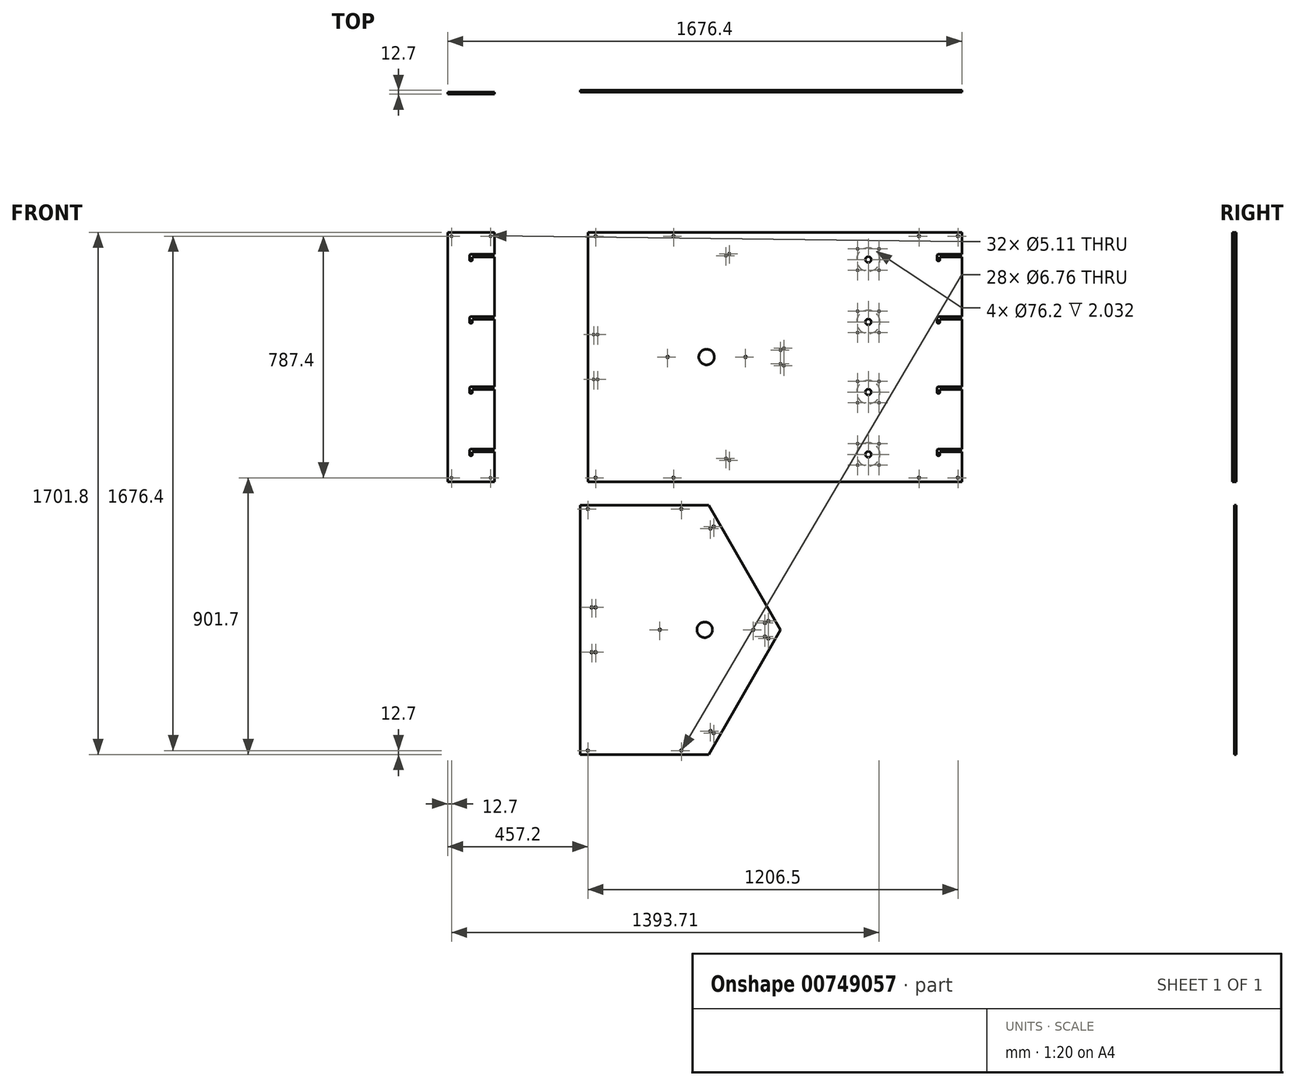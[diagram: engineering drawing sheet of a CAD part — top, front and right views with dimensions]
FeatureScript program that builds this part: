
annotation { "Feature Type Name" : "Feature", "Feature Type Description" : "" }
export const myFeature = defineFeature(function(context is Context, id is Id, definition is map)
    precondition{}
    {
        {
            var Q0;
            Q0=qCreatedBy(makeId("Front.planeOp"),FACE);
            var sketch = newSketch(context, id + "F0", { "sketchPlane" : qUnion([Q0])});
            skLineSegment(sketch, "E0.bottom", {"start": v(0, 0) * mm, "end": v(1219.2, 0) * mm});
            skLineSegment(sketch, "E0.top", {"start": v(53.97, 812.8) * mm, "end": v(1219.2, 812.8) * mm});
            skLineSegment(sketch, "E0.left", {"start": v(0, 0) * mm, "end": v(0, 47.62) * mm});
            skLineSegment(sketch, "E0.right", {"start": v(1219.2, 0) * mm, "end": v(1219.2, 812.8) * mm});
            skLineSegment(sketch, "E1.trimOffspring", {"start": v(0, 104.78) * mm, "end": v(0, 406.4) * mm});
            skLineSegment(sketch, "E2", {"start": v(53.97, 812.8) * mm, "end": v(0, 812.8) * mm});
            skLineSegment(sketch, "E3", {"start": v(0, 812.8) * mm, "end": v(0, 406.4) * mm});
            skLineSegment(sketch, "E4", {"start": v(0, 104.78) * mm, "end": v(0, 47.62) * mm});
            skLineSegment(sketch, "E5", {"start": v(1219.2, 406.4) * mm, "end": v(0, 406.4) * mm, "construction": true});
            skLineSegment(sketch, "E6.left", {"start": v(0, 508) * mm, "end": v(0, 304.8) * mm});
            skSolve(sketch);
        }
        {
            var Q0;
            Q0 = qSketchRegion(id + "F0", true);
            extrude(context, id + "F1", {"entities" : qUnion([Q0]), "oppositeDirection" : true, "depth" : 6.35 * mm, "offsetDistance" : 25.4 * mm});
        }
        {
            var Q0;
            Q0=makeQuery(id+"F1.opExtrude","CAP_FACE",FACE,{"disambiguationData":[OSD([sQuery(id+"F0.wireOp",EDGE,"E0.bottom"),sQuery(id+"F0.wireOp",EDGE,"E0.top"),sQuery(id+"F0.wireOp",EDGE,"E0.left"),sQuery(id+"F0.wireOp",EDGE,"E0.right"),sQuery(id+"F0.wireOp",EDGE,"GyBe3EqK-cSh5-v1t1-OVTD-ahxNfT15hAsZ.top"),sQuery(id+"F0.wireOp",EDGE,"GyBe3EqK-cSh5-v1t1-OVTD-ahxNfT15hAsZ.right"),sQuery(id+"F0.wireOp",EDGE,"EnS1OxtH-lJOK-UO4v-DnPg-Mq8DwQejlwmV.bottom"),sQuery(id+"F0.wireOp",EDGE,"EnS1OxtH-lJOK-UO4v-DnPg-Mq8DwQejlwmV.top"),sQuery(id+"F0.wireOp",EDGE,"EnS1OxtH-lJOK-UO4v-DnPg-Mq8DwQejlwmV.right"),sQuery(id+"F0.wireOp",EDGE,"E1.trimOffspring")])],"isStart":true});
            var sketch = newSketch(context, id + "F2", { "sketchPlane" : qUnion([Q0])});
            skLineSegment(sketch, "E7", {"start": v(1219.2, 406.4) * mm, "end": v(0, 406.4) * mm, "construction": true});
            skLineSegment(sketch, "E8", {"start": v(406.4, 0) * mm, "end": v(641.04, 406.4) * mm, "construction": true});
            skLineSegment(sketch, "E9", {"start": v(641.04, 406.4) * mm, "end": v(406.4, 812.8) * mm, "construction": true});
            skPoint(sketch, "E10", {"position": v(450.4, 76.2) * mm});
            skPoint(sketch, "E11", {"position": v(628.2, 384.16) * mm});
            skLineSegment(sketch, "E12", {"start": v(421.06, 0) * mm, "end": v(655.7, 406.4) * mm, "construction": true});
            skLineSegment(sketch, "E13", {"start": v(450.4, 76.2) * mm, "end": v(461.4, 69.85) * mm, "construction": true});
            skLineSegment(sketch, "E14", {"start": v(628.2, 384.16) * mm, "end": v(639.2, 377.8) * mm, "construction": true});
            skPoint(sketch, "E15", {"position": v(639.2, 377.8) * mm});
            skPoint(sketch, "E16", {"position": v(461.4, 69.85) * mm});
            skPoint(sketch, "E17.MirrorP", {"position": v(628.2, 428.64) * mm});
            skPoint(sketch, "E18.MirrorP", {"position": v(639.2, 435) * mm});
            skPoint(sketch, "E19.MirrorP", {"position": v(461.4, 742.95) * mm});
            skPoint(sketch, "E20.MirrorP", {"position": v(450.4, 736.6) * mm});
            skLineSegment(sketch, "E21", {"start": v(25.4, 812.8) * mm, "end": v(25.4, 0) * mm, "construction": true});
            skPoint(sketch, "E22", {"position": v(19.05, 479.43) * mm});
            skPoint(sketch, "E23.MirrorP", {"position": v(31.75, 479.43) * mm});
            skPoint(sketch, "E24.MirrorP", {"position": v(19.05, 333.38) * mm});
            skPoint(sketch, "E25.MirrorP", {"position": v(31.75, 333.38) * mm});
            skSolve(sketch);
        }
        {
            var Q0;
            Q0=sQuery(id+"F2.wireOp",VERTEX,"1f2a52ec-5eff-4167-b222-c35b7b9c67ac0.MirrorP");
            var Q1;
            Q1=sQuery(id+"F2.wireOp",VERTEX,"6a59a917-cddb-4341-b7b2-614a49050ed80.MirrorP");
            var Q2;
            Q2=sQuery(id+"F2.wireOp",VERTEX,"aa4bf911-a7ad-4460-99d6-e9a0e6d8d9e1");
            var Q3;
            Q3=sQuery(id+"F2.wireOp",VERTEX,"df6880c4-e116-4ecd-98e9-50faa79850ba");
            var Q4;
            Q4=sQuery(id+"F2.wireOp",VERTEX,"cc07dee6-96a4-47fe-b955-c56ce8794536");
            var Q5;
            Q5=sQuery(id+"F2.wireOp",VERTEX,"bf74a886-9e41-4cef-b4e5-6878ea112274");
            var Q6;
            Q6=sQuery(id+"F2.wireOp",VERTEX,"cd125775-8d29-4c7f-8b29-d38cd7ae1aca0.MirrorP");
            var Q7;
            Q7=sQuery(id+"F2.wireOp",VERTEX,"78534849-580e-4fdc-a252-b2fe906053fd0.MirrorP");
            var Q8;
            Q8=sQuery(id+"F2.wireOp",VERTEX,"19cf28b5-96e7-4680-8611-90bc4ffa497d0.MirrorP");
            var Q9;
            Q9=sQuery(id+"F2.wireOp",VERTEX,"6d1cc372-7a9e-40b0-874d-be10c53de4300.MirrorP");
            var Q10;
            Q10=sQuery(id+"F2.wireOp",VERTEX,"eb98779b-e2d4-40db-b351-41a48d78d36b0.MirrorP");
            var Q11;
            Q11=sQuery(id+"F2.wireOp",VERTEX,"24989635-3b41-4970-88e9-65368ecc07f30.MirrorP");
            var Q12;
            Q12=sQuery(id+"F2.wireOp",VERTEX,"E10");
            var Q13;
            Q13=sQuery(id+"F2.wireOp",VERTEX,"E16");
            var Q14;
            Q14=sQuery(id+"F2.wireOp",VERTEX,"E15");
            var Q15;
            Q15=sQuery(id+"F2.wireOp",VERTEX,"E11");
            var Q16;
            Q16=sQuery(id+"F2.wireOp",VERTEX,"E18.MirrorP");
            var Q17;
            Q17=sQuery(id+"F2.wireOp",VERTEX,"E17.MirrorP");
            var Q18;
            Q18=sQuery(id+"F2.wireOp",VERTEX,"E19.MirrorP");
            var Q19;
            Q19=sQuery(id+"F2.wireOp",VERTEX,"E20.MirrorP");
            var Q20;
            Q20=sQuery(id+"F2.wireOp",VERTEX,"E25.MirrorP");
            var Q21;
            Q21=sQuery(id+"F2.wireOp",VERTEX,"E22");
            var Q22;
            Q22=sQuery(id+"F2.wireOp",VERTEX,"E23.MirrorP");
            var Q23;
            Q23=sQuery(id+"F2.wireOp",VERTEX,"E24.MirrorP");
            var Q24;
            Q24=makeQuery(id+"F1.opExtrude","SWEPT_BODY",BODY,{"disambiguationData":[OSD([sQuery(id+"F0.wireOp",EDGE,"E0.bottom"),sQuery(id+"F0.wireOp",EDGE,"E0.top"),sQuery(id+"F0.wireOp",EDGE,"E0.left"),sQuery(id+"F0.wireOp",EDGE,"E0.right"),sQuery(id+"F0.wireOp",EDGE,"GyBe3EqK-cSh5-v1t1-OVTD-ahxNfT15hAsZ.top"),sQuery(id+"F0.wireOp",EDGE,"GyBe3EqK-cSh5-v1t1-OVTD-ahxNfT15hAsZ.right"),sQuery(id+"F0.wireOp",EDGE,"EnS1OxtH-lJOK-UO4v-DnPg-Mq8DwQejlwmV.bottom"),sQuery(id+"F0.wireOp",EDGE,"EnS1OxtH-lJOK-UO4v-DnPg-Mq8DwQejlwmV.top"),sQuery(id+"F0.wireOp",EDGE,"EnS1OxtH-lJOK-UO4v-DnPg-Mq8DwQejlwmV.right"),sQuery(id+"F0.wireOp",EDGE,"E1.trimOffspring")])]});
            hole(context, id + "F3", {"style" : HoleStyle.SIMPLE, "endStyle" : HoleEndStyle.BLIND, "standardTappedOrClearance" : lookupTablePath({ "standard" : "ANSI", "engagement" : "75%", "pitch" : "20 tpi", "size" : "1/4", "type" : "Tapped" }), "standardBlindInLast" : lookupTablePath({ "standard" : "ANSI", "engagement" : "75%", "pitch" : "20 tpi", "size" : "1/4", "type" : "Tapped" }), "holeDiameter" : 5.1 * mm, "majorDiameter" : 6.35 * mm, "showTappedDepth" : true, "holeDepth" : 26.06 * mm, "isTappedThrough" : true, "tappedDepth" : 22.25 * mm, "tapClearance" : 3, "locations" : qUnion([Q0, Q1, Q2, Q3, Q4, Q5, Q6, Q7, Q8, Q9, Q10, Q11, Q12, Q13, Q14, Q15, Q16, Q17, Q18, Q19, Q20, Q21, Q22, Q23]), "scope" : qUnion([Q24])});
        }
        {
            var Q0;
            Q0=makeQuery(id+"F1.opExtrude","CAP_FACE",FACE,{"disambiguationData":[OSD([sQuery(id+"F0.wireOp",EDGE,"E0.bottom"),sQuery(id+"F0.wireOp",EDGE,"E0.top"),sQuery(id+"F0.wireOp",EDGE,"E0.left"),sQuery(id+"F0.wireOp",EDGE,"E0.right"),sQuery(id+"F0.wireOp",EDGE,"GyBe3EqK-cSh5-v1t1-OVTD-ahxNfT15hAsZ.top"),sQuery(id+"F0.wireOp",EDGE,"GyBe3EqK-cSh5-v1t1-OVTD-ahxNfT15hAsZ.right"),sQuery(id+"F0.wireOp",EDGE,"EnS1OxtH-lJOK-UO4v-DnPg-Mq8DwQejlwmV.bottom"),sQuery(id+"F0.wireOp",EDGE,"EnS1OxtH-lJOK-UO4v-DnPg-Mq8DwQejlwmV.top"),sQuery(id+"F0.wireOp",EDGE,"EnS1OxtH-lJOK-UO4v-DnPg-Mq8DwQejlwmV.right"),sQuery(id+"F0.wireOp",EDGE,"E1.trimOffspring")])],"isStart":true});
            var sketch = newSketch(context, id + "F4", { "sketchPlane" : qUnion([Q0])});
            skLineSegment(sketch, "E26", {"start": v(1219.2, 406.4) * mm, "end": v(0, 406.4) * mm, "construction": true});
            skLineSegment(sketch, "E27", {"start": v(1219.2, 736.6) * mm, "end": v(1143, 736.6) * mm});
            skLineSegment(sketch, "E28", {"start": v(1143, 736.6) * mm, "end": v(1143, 723.9) * mm});
            skArc(sketch, "E29.0.startCap", {"start": v(1219.2, 741.36) * mm, "mid": v(1223.96, 736.6) * mm, "end": v(1219.2, 731.84) * mm});
            skArc(sketch, "E29.0.endCap", {"start": v(1143, 731.84) * mm, "mid": v(1138.24, 736.6) * mm, "end": v(1143, 741.36) * mm});
            skLineSegment(sketch, "E29.0.left", {"start": v(1219.2, 731.84) * mm, "end": v(1143, 731.84) * mm});
            skLineSegment(sketch, "E29.0.right", {"start": v(1219.2, 741.36) * mm, "end": v(1143, 741.36) * mm});
            skArc(sketch, "E29.1.startCap", {"start": v(1138.24, 736.6) * mm, "mid": v(1143, 741.36) * mm, "end": v(1147.76, 736.6) * mm});
            skArc(sketch, "E29.1.endCap", {"start": v(1147.76, 723.9) * mm, "mid": v(1143, 719.14) * mm, "end": v(1138.24, 723.9) * mm});
            skLineSegment(sketch, "E29.1.left", {"start": v(1147.76, 736.6) * mm, "end": v(1147.76, 723.9) * mm});
            skLineSegment(sketch, "E29.1.right", {"start": v(1138.24, 736.6) * mm, "end": v(1138.24, 723.9) * mm});
            skLineSegment(sketch, "E30", {"start": v(1219.2, 533.4) * mm, "end": v(1143, 533.4) * mm});
            skLineSegment(sketch, "E31", {"start": v(1143, 533.4) * mm, "end": v(1143, 520.7) * mm});
            skArc(sketch, "E32.0.startCap", {"start": v(1219.2, 538.16) * mm, "mid": v(1223.96, 533.4) * mm, "end": v(1219.2, 528.64) * mm});
            skArc(sketch, "E32.0.endCap", {"start": v(1143, 528.64) * mm, "mid": v(1138.24, 533.4) * mm, "end": v(1143, 538.16) * mm});
            skLineSegment(sketch, "E32.0.left", {"start": v(1219.2, 528.64) * mm, "end": v(1143, 528.64) * mm});
            skLineSegment(sketch, "E32.0.right", {"start": v(1219.2, 538.16) * mm, "end": v(1143, 538.16) * mm});
            skArc(sketch, "E32.1.startCap", {"start": v(1138.24, 533.4) * mm, "mid": v(1143, 538.16) * mm, "end": v(1147.76, 533.4) * mm});
            skArc(sketch, "E32.1.endCap", {"start": v(1147.76, 520.7) * mm, "mid": v(1143, 515.94) * mm, "end": v(1138.24, 520.7) * mm});
            skLineSegment(sketch, "E32.1.left", {"start": v(1147.76, 533.4) * mm, "end": v(1147.76, 520.7) * mm});
            skLineSegment(sketch, "E32.1.right", {"start": v(1138.24, 533.4) * mm, "end": v(1138.24, 520.7) * mm});
            skLineSegment(sketch, "E33", {"start": v(0, 622.3) * mm, "end": v(1219.2, 622.3) * mm, "construction": true});
            skLineSegment(sketch, "E34", {"start": v(0, 190.5) * mm, "end": v(1219.2, 190.5) * mm, "construction": true});
            skLineSegment(sketch, "E35", {"start": v(1219.2, 304.8) * mm, "end": v(1143, 304.8) * mm});
            skLineSegment(sketch, "E36", {"start": v(1143, 304.8) * mm, "end": v(1143, 292.1) * mm});
            skArc(sketch, "E37.0.startCap", {"start": v(1219.2, 309.56) * mm, "mid": v(1223.96, 304.8) * mm, "end": v(1219.2, 300.04) * mm});
            skArc(sketch, "E37.0.endCap", {"start": v(1143, 300.04) * mm, "mid": v(1138.24, 304.8) * mm, "end": v(1143, 309.56) * mm});
            skLineSegment(sketch, "E37.0.left", {"start": v(1219.2, 300.04) * mm, "end": v(1143, 300.04) * mm});
            skLineSegment(sketch, "E37.0.right", {"start": v(1219.2, 309.56) * mm, "end": v(1143, 309.56) * mm});
            skArc(sketch, "E37.1.startCap", {"start": v(1138.24, 304.8) * mm, "mid": v(1143, 309.56) * mm, "end": v(1147.76, 304.8) * mm});
            skArc(sketch, "E37.1.endCap", {"start": v(1147.76, 292.1) * mm, "mid": v(1143, 287.34) * mm, "end": v(1138.24, 292.1) * mm});
            skLineSegment(sketch, "E37.1.left", {"start": v(1147.76, 304.8) * mm, "end": v(1147.76, 292.1) * mm});
            skLineSegment(sketch, "E37.1.right", {"start": v(1138.24, 304.8) * mm, "end": v(1138.24, 292.1) * mm});
            skLineSegment(sketch, "E38", {"start": v(1219.2, 101.6) * mm, "end": v(1143, 101.6) * mm});
            skLineSegment(sketch, "E39", {"start": v(1143, 101.6) * mm, "end": v(1143, 88.9) * mm});
            skArc(sketch, "E40.0.startCap", {"start": v(1219.2, 106.36) * mm, "mid": v(1223.96, 101.6) * mm, "end": v(1219.2, 96.84) * mm});
            skArc(sketch, "E40.0.endCap", {"start": v(1143, 96.84) * mm, "mid": v(1138.24, 101.6) * mm, "end": v(1143, 106.36) * mm});
            skLineSegment(sketch, "E40.0.left", {"start": v(1219.2, 96.84) * mm, "end": v(1143, 96.84) * mm});
            skLineSegment(sketch, "E40.0.right", {"start": v(1219.2, 106.36) * mm, "end": v(1143, 106.36) * mm});
            skArc(sketch, "E40.1.startCap", {"start": v(1138.24, 101.6) * mm, "mid": v(1143, 106.36) * mm, "end": v(1147.76, 101.6) * mm});
            skArc(sketch, "E40.1.endCap", {"start": v(1147.76, 88.9) * mm, "mid": v(1143, 84.14) * mm, "end": v(1138.24, 88.9) * mm});
            skLineSegment(sketch, "E40.1.left", {"start": v(1147.76, 101.6) * mm, "end": v(1147.76, 88.9) * mm});
            skLineSegment(sketch, "E40.1.right", {"start": v(1138.24, 101.6) * mm, "end": v(1138.24, 88.9) * mm});
            skSolve(sketch);
        }
        {
            var Q0;
            Q0 = qSketchRegion(id + "F4", true);
            extrude(context, id + "F5", {"entities" : qUnion([Q0]), "operationType" : NewBodyOperationType.REMOVE, "oppositeDirection" : true, "depth" : 25.4 * mm, "offsetDistance" : 25.4 * mm});
        }
        {
            var Q0;
            Q0=makeQuery(id+"F1.opExtrude","CAP_FACE",FACE,{"disambiguationData":[OSD([sQuery(id+"F0.wireOp",EDGE,"E0.bottom"),sQuery(id+"F0.wireOp",EDGE,"E0.top"),sQuery(id+"F0.wireOp",EDGE,"E0.left"),sQuery(id+"F0.wireOp",EDGE,"E0.right"),sQuery(id+"F0.wireOp",EDGE,"E1.trimOffspring"),sQuery(id+"F0.wireOp",EDGE,"E2"),sQuery(id+"F0.wireOp",EDGE,"E3"),sQuery(id+"F0.wireOp",EDGE,"E4")])],"isStart":true});
            var sketch = newSketch(context, id + "F6", { "sketchPlane" : qUnion([Q0])});
            skLineSegment(sketch, "E41", {"start": v(0, 0) * mm, "end": v(234.64, 406.4) * mm, "construction": true});
            skLineSegment(sketch, "E42", {"start": v(234.64, 406.4) * mm, "end": v(0, 812.8) * mm, "construction": true});
            skLineSegment(sketch, "E43", {"start": v(304.8, 812.8) * mm, "end": v(539.44, 406.4) * mm, "construction": true});
            skLineSegment(sketch, "E44", {"start": v(539.44, 406.4) * mm, "end": v(304.8, 0) * mm, "construction": true});
            skLineSegment(sketch, "E45", {"start": v(234.64, 406.4) * mm, "end": v(539.44, 406.4) * mm, "construction": true});
            skLineSegment(sketch, "E46", {"start": v(152.4, 0) * mm, "end": v(152.4, 812.8) * mm, "construction": true});
            skPoint(sketch, "E47", {"position": v(25.4, 12.7) * mm});
            skLineSegment(sketch, "E48", {"start": v(387.04, 670.36) * mm, "end": v(387.04, 142.44) * mm, "construction": true});
            skPoint(sketch, "E48.startSnap0", {"position": v(387.04, 406.4) * mm});
            skPoint(sketch, "E49", {"position": v(514.04, 406.4) * mm});
            skPoint(sketch, "E50.MirrorP", {"position": v(279.4, 12.7) * mm});
            skPoint(sketch, "E51.MirrorP", {"position": v(279.4, 800.1) * mm});
            skPoint(sketch, "E52.MirrorP", {"position": v(25.4, 800.1) * mm});
            skPoint(sketch, "E53.MirrorP", {"position": v(260.04, 406.4) * mm});
            skCircle(sketch, "E54", {"center": v(387.04, 406.4) * mm, "radius": 25.4 * mm});
            skSolve(sketch);
        }
        {
            var Q0;
            Q0=sQuery(id+"F6.wireOp",VERTEX,"E52.MirrorP");
            var Q1;
            Q1=sQuery(id+"F6.wireOp",VERTEX,"E51.MirrorP");
            var Q2;
            Q2=sQuery(id+"F6.wireOp",VERTEX,"E47");
            var Q3;
            Q3=sQuery(id+"F6.wireOp",VERTEX,"E50.MirrorP");
            var Q4;
            Q4=sQuery(id+"F6.wireOp",VERTEX,"E53.MirrorP");
            var Q5;
            Q5=sQuery(id+"F6.wireOp",VERTEX,"E49");
            var Q6;
            Q6=makeQuery(id+"F1.opExtrude","SWEPT_BODY",BODY,{"disambiguationData":[OSD([sQuery(id+"F0.wireOp",EDGE,"E0.bottom"),sQuery(id+"F0.wireOp",EDGE,"E0.top"),sQuery(id+"F0.wireOp",EDGE,"E0.left"),sQuery(id+"F0.wireOp",EDGE,"E0.right"),sQuery(id+"F0.wireOp",EDGE,"E1.trimOffspring"),sQuery(id+"F0.wireOp",EDGE,"E2"),sQuery(id+"F0.wireOp",EDGE,"E3"),sQuery(id+"F0.wireOp",EDGE,"E4")])]});
            hole(context, id + "F7", {"style" : HoleStyle.SIMPLE, "endStyle" : HoleEndStyle.BLIND, "standardTappedOrClearance" : lookupTablePath({ "fit" : "Normal (ASME)", "standard" : "ANSI", "size" : "1/4", "type" : "Clearance" }), "standardBlindInLast" : lookupTablePath({ "fit" : "Free", "standard" : "ANSI", "size" : "1/4", "type" : "Clearance" }), "holeDiameter" : 6.76 * mm, "majorDiameter" : 6.35 * mm, "holeDepth" : 26.06 * mm, "isTappedThrough" : true, "tappedDepth" : 22.25 * mm, "tapClearance" : 3, "locations" : qUnion([Q0, Q1, Q2, Q3, Q4, Q5]), "scope" : qUnion([Q6])});
        }
        {
            var Q0;
            Q0=qCreatedBy(makeId("Front.planeOp"),FACE);
            var sketch = newSketch(context, id + "F8", { "sketchPlane" : qUnion([Q0])});
            skLineSegment(sketch, "E55.bottom", {"start": v(-304.8, 0) * mm, "end": v(-457.2, 0) * mm});
            skLineSegment(sketch, "E55.top", {"start": v(-304.8, 812.8) * mm, "end": v(-457.2, 812.8) * mm});
            skLineSegment(sketch, "E55.left", {"start": v(-304.8, 0) * mm, "end": v(-304.8, 812.8) * mm});
            skLineSegment(sketch, "E55.right", {"start": v(-457.2, 0) * mm, "end": v(-457.2, 812.8) * mm});
            skLineSegment(sketch, "E56", {"start": v(-304.8, 406.4) * mm, "end": v(-457.2, 406.4) * mm, "construction": true});
            skLineSegment(sketch, "E57", {"start": v(-304.8, 622.3) * mm, "end": v(-457.2, 622.3) * mm, "construction": true});
            skLineSegment(sketch, "E58", {"start": v(-304.8, 190.5) * mm, "end": v(-457.2, 190.5) * mm, "construction": true});
            skLineSegment(sketch, "E59", {"start": v(-304.8, 736.6) * mm, "end": v(-381, 736.6) * mm});
            skLineSegment(sketch, "E60", {"start": v(-381, 736.6) * mm, "end": v(-381, 723.9) * mm});
            skArc(sketch, "E61.0.startCap", {"start": v(-304.8, 741.36) * mm, "mid": v(-300.04, 736.6) * mm, "end": v(-304.8, 731.84) * mm});
            skArc(sketch, "E61.0.endCap", {"start": v(-381, 731.84) * mm, "mid": v(-385.76, 736.6) * mm, "end": v(-381, 741.36) * mm});
            skLineSegment(sketch, "E61.0.left", {"start": v(-304.8, 731.84) * mm, "end": v(-381, 731.84) * mm});
            skLineSegment(sketch, "E61.0.right", {"start": v(-304.8, 741.36) * mm, "end": v(-381, 741.36) * mm});
            skArc(sketch, "E61.1.startCap", {"start": v(-385.76, 736.6) * mm, "mid": v(-381, 741.36) * mm, "end": v(-376.24, 736.6) * mm});
            skArc(sketch, "E61.1.endCap", {"start": v(-376.24, 723.9) * mm, "mid": v(-381, 719.14) * mm, "end": v(-385.76, 723.9) * mm});
            skLineSegment(sketch, "E61.1.left", {"start": v(-376.24, 736.6) * mm, "end": v(-376.24, 723.9) * mm});
            skLineSegment(sketch, "E61.1.right", {"start": v(-385.76, 736.6) * mm, "end": v(-385.76, 723.9) * mm});
            skLineSegment(sketch, "E62", {"start": v(-304.8, 533.4) * mm, "end": v(-381, 533.4) * mm});
            skLineSegment(sketch, "E63", {"start": v(-381, 533.4) * mm, "end": v(-381, 520.7) * mm});
            skArc(sketch, "E64.0.startCap", {"start": v(-304.8, 538.16) * mm, "mid": v(-300.04, 533.4) * mm, "end": v(-304.8, 528.64) * mm});
            skArc(sketch, "E64.0.endCap", {"start": v(-381, 528.64) * mm, "mid": v(-385.76, 533.4) * mm, "end": v(-381, 538.16) * mm});
            skLineSegment(sketch, "E64.0.left", {"start": v(-304.8, 528.64) * mm, "end": v(-381, 528.64) * mm});
            skLineSegment(sketch, "E64.0.right", {"start": v(-304.8, 538.16) * mm, "end": v(-381, 538.16) * mm});
            skArc(sketch, "E64.1.startCap", {"start": v(-385.76, 533.4) * mm, "mid": v(-381, 538.16) * mm, "end": v(-376.24, 533.4) * mm});
            skArc(sketch, "E64.1.endCap", {"start": v(-376.24, 520.7) * mm, "mid": v(-381, 515.94) * mm, "end": v(-385.76, 520.7) * mm});
            skLineSegment(sketch, "E64.1.left", {"start": v(-376.24, 533.4) * mm, "end": v(-376.24, 520.7) * mm});
            skLineSegment(sketch, "E64.1.right", {"start": v(-385.76, 533.4) * mm, "end": v(-385.76, 520.7) * mm});
            skLineSegment(sketch, "E65", {"start": v(-304.8, 304.8) * mm, "end": v(-381, 304.8) * mm});
            skLineSegment(sketch, "E66", {"start": v(-381, 304.8) * mm, "end": v(-381, 292.1) * mm});
            skArc(sketch, "E67.0.startCap", {"start": v(-304.8, 309.56) * mm, "mid": v(-300.04, 304.8) * mm, "end": v(-304.8, 300.04) * mm});
            skArc(sketch, "E67.0.endCap", {"start": v(-381, 300.04) * mm, "mid": v(-385.76, 304.8) * mm, "end": v(-381, 309.56) * mm});
            skLineSegment(sketch, "E67.0.left", {"start": v(-304.8, 300.04) * mm, "end": v(-381, 300.04) * mm});
            skLineSegment(sketch, "E67.0.right", {"start": v(-304.8, 309.56) * mm, "end": v(-381, 309.56) * mm});
            skArc(sketch, "E67.1.startCap", {"start": v(-385.76, 304.8) * mm, "mid": v(-381, 309.56) * mm, "end": v(-376.24, 304.8) * mm});
            skArc(sketch, "E67.1.endCap", {"start": v(-376.24, 292.1) * mm, "mid": v(-381, 287.34) * mm, "end": v(-385.76, 292.1) * mm});
            skLineSegment(sketch, "E67.1.left", {"start": v(-376.24, 304.8) * mm, "end": v(-376.24, 292.1) * mm});
            skLineSegment(sketch, "E67.1.right", {"start": v(-385.76, 304.8) * mm, "end": v(-385.76, 292.1) * mm});
            skLineSegment(sketch, "E68", {"start": v(-304.8, 101.6) * mm, "end": v(-381, 101.6) * mm});
            skLineSegment(sketch, "E69", {"start": v(-381, 101.6) * mm, "end": v(-381, 88.9) * mm});
            skArc(sketch, "E70.0.startCap", {"start": v(-304.8, 106.36) * mm, "mid": v(-300.04, 101.6) * mm, "end": v(-304.8, 96.84) * mm});
            skArc(sketch, "E70.0.endCap", {"start": v(-381, 96.84) * mm, "mid": v(-385.76, 101.6) * mm, "end": v(-381, 106.36) * mm});
            skLineSegment(sketch, "E70.0.left", {"start": v(-304.8, 96.84) * mm, "end": v(-381, 96.84) * mm});
            skLineSegment(sketch, "E70.0.right", {"start": v(-304.8, 106.36) * mm, "end": v(-381, 106.36) * mm});
            skArc(sketch, "E70.1.startCap", {"start": v(-385.76, 101.6) * mm, "mid": v(-381, 106.36) * mm, "end": v(-376.24, 101.6) * mm});
            skArc(sketch, "E70.1.endCap", {"start": v(-376.24, 88.9) * mm, "mid": v(-381, 84.14) * mm, "end": v(-385.76, 88.9) * mm});
            skLineSegment(sketch, "E70.1.left", {"start": v(-376.24, 101.6) * mm, "end": v(-376.24, 88.9) * mm});
            skLineSegment(sketch, "E70.1.right", {"start": v(-385.76, 101.6) * mm, "end": v(-385.76, 88.9) * mm});
            skLineSegment(sketch, "E71", {"start": v(-381, 812.8) * mm, "end": v(-381, 0) * mm, "construction": true});
            skPoint(sketch, "E72", {"position": v(-444.5, 12.7) * mm});
            skPoint(sketch, "E73.MirrorP", {"position": v(-444.5, 800.1) * mm});
            skPoint(sketch, "E74.MirrorP", {"position": v(-317.5, 800.1) * mm});
            skPoint(sketch, "E75.MirrorP", {"position": v(-317.5, 12.7) * mm});
            skSolve(sketch);
        }
        {
            var Q0;
            {var subQ14=sQuery(id+"F8.wireOp",EDGE,"E55.bottom");Q0=makeQuery(id+"F8.imprint","IMPRINT",FACE,{"disambiguationData":[TD([[makeQuery(id+"F8.imprint","IMPRINT",EDGE,{"derivedFrom":subQ14}),-1.0]])]});}
            extrude(context, id + "F9", {"entities" : qUnion([Q0]), "depth" : 6.35 * mm, "offsetDistance" : 25.4 * mm});
        }
        {
            var Q0;
            Q0=makeQuery(id+"F1.opExtrude","CAP_FACE",FACE,{"disambiguationData":[OSD([sQuery(id+"F0.wireOp",EDGE,"E0.bottom"),sQuery(id+"F0.wireOp",EDGE,"E0.top"),sQuery(id+"F0.wireOp",EDGE,"E0.left"),sQuery(id+"F0.wireOp",EDGE,"E0.right"),sQuery(id+"F0.wireOp",EDGE,"E1.trimOffspring"),sQuery(id+"F0.wireOp",EDGE,"E2"),sQuery(id+"F0.wireOp",EDGE,"E3"),sQuery(id+"F0.wireOp",EDGE,"E4"),sQuery(id+"F0.wireOp",EDGE,"E6.bottom"),sQuery(id+"F0.wireOp",EDGE,"E6.top"),sQuery(id+"F0.wireOp",EDGE,"E6.right")])],"isStart":false});
            var sketch = newSketch(context, id + "F10", { "sketchPlane" : qUnion([Q0])});
            skLineSegment(sketch, "E76", {"start": v(-914.4, 812.8) * mm, "end": v(-914.4, 0) * mm, "construction": true});
            skLineSegment(sketch, "E77", {"start": v(-1219.2, 622.3) * mm, "end": v(-914.4, 622.3) * mm, "construction": true});
            skCircle(sketch, "E78", {"center": v(-914.4, 723.9) * mm, "radius": 9.53 * mm});
            skCircle(sketch, "E79.MirrorC", {"center": v(-914.4, 520.7) * mm, "radius": 9.53 * mm});
            skCircle(sketch, "E80", {"center": v(-914.4, 723.9) * mm, "radius": 49.23 * mm, "construction": true});
            skLineSegment(sketch, "E81.bottom", {"start": v(-871.22, 680.72) * mm, "end": v(-957.58, 680.72) * mm, "construction": true});
            skLineSegment(sketch, "E81.top", {"start": v(-871.22, 767.08) * mm, "end": v(-957.58, 767.08) * mm, "construction": true});
            skLineSegment(sketch, "E81.left", {"start": v(-871.22, 680.72) * mm, "end": v(-871.22, 767.08) * mm, "construction": true});
            skLineSegment(sketch, "E81.right", {"start": v(-957.58, 680.72) * mm, "end": v(-957.58, 767.08) * mm, "construction": true});
            skLineSegment(sketch, "E82", {"start": v(-871.22, 767.08) * mm, "end": v(-957.58, 680.72) * mm, "construction": true});
            skLineSegment(sketch, "E83", {"start": v(-957.58, 767.08) * mm, "end": v(-871.22, 680.72) * mm, "construction": true});
            skPoint(sketch, "E84", {"position": v(-949.2, 758.7) * mm});
            skPoint(sketch, "E85", {"position": v(-879.6, 758.7) * mm});
            skPoint(sketch, "E86", {"position": v(-879.6, 689.1) * mm});
            skPoint(sketch, "E87", {"position": v(-949.2, 689.1) * mm});
            skPoint(sketch, "E88.MirrorP", {"position": v(-949.2, 555.5) * mm});
            skPoint(sketch, "E89.MirrorP", {"position": v(-879.6, 555.5) * mm});
            skPoint(sketch, "E90.MirrorP", {"position": v(-879.6, 485.9) * mm});
            skPoint(sketch, "E91.MirrorP", {"position": v(-949.2, 485.9) * mm});
            skLineSegment(sketch, "E92", {"start": v(0, 406.4) * mm, "end": v(-1219.2, 406.4) * mm, "construction": true});
            skPoint(sketch, "E93.MirrorP", {"position": v(-949.2, 326.9) * mm});
            skPoint(sketch, "E94.MirrorP", {"position": v(-879.6, 326.9) * mm});
            skPoint(sketch, "E95.MirrorP", {"position": v(-879.6, 257.3) * mm});
            skPoint(sketch, "E96.MirrorP", {"position": v(-949.2, 257.3) * mm});
            skCircle(sketch, "E97.MirrorC", {"center": v(-914.4, 292.1) * mm, "radius": 9.53 * mm});
            skPoint(sketch, "E98.MirrorP", {"position": v(-879.6, 123.7) * mm});
            skPoint(sketch, "E99.MirrorP", {"position": v(-879.6, 54.1) * mm});
            skPoint(sketch, "E100.MirrorP", {"position": v(-949.2, 54.1) * mm});
            skPoint(sketch, "E101.MirrorP", {"position": v(-949.2, 123.7) * mm});
            skPoint(sketch, "E102.MirrorP", {"position": v(-914.4, 88.9) * mm});
            skCircle(sketch, "E103.MirrorC", {"center": v(-914.4, 88.9) * mm, "radius": 9.53 * mm});
            skSolve(sketch);
        }
        {
            var Q0;
            Q0 = qSketchRegion(id + "F10", true);
            extrude(context, id + "F11", {"entities" : qUnion([Q0]), "operationType" : NewBodyOperationType.REMOVE, "oppositeDirection" : true, "depth" : 25.4 * mm, "offsetDistance" : 25.4 * mm});
        }
        {
            var Q0;
            Q0=sQuery(id+"F10.wireOp",VERTEX,"E87");
            var Q1;
            Q1=sQuery(id+"F10.wireOp",VERTEX,"E86");
            var Q2;
            Q2=sQuery(id+"F10.wireOp",VERTEX,"E85");
            var Q3;
            Q3=sQuery(id+"F10.wireOp",VERTEX,"E84");
            var Q4;
            Q4=sQuery(id+"F10.wireOp",VERTEX,"E88.MirrorP");
            var Q5;
            Q5=sQuery(id+"F10.wireOp",VERTEX,"E89.MirrorP");
            var Q6;
            Q6=sQuery(id+"F10.wireOp",VERTEX,"E90.MirrorP");
            var Q7;
            Q7=sQuery(id+"F10.wireOp",VERTEX,"E91.MirrorP");
            var Q8;
            Q8=sQuery(id+"F10.wireOp",VERTEX,"E93.MirrorP");
            var Q9;
            Q9=sQuery(id+"F10.wireOp",VERTEX,"E94.MirrorP");
            var Q10;
            Q10=sQuery(id+"F10.wireOp",VERTEX,"E95.MirrorP");
            var Q11;
            Q11=sQuery(id+"F10.wireOp",VERTEX,"E96.MirrorP");
            var Q12;
            Q12=sQuery(id+"F10.wireOp",VERTEX,"E98.MirrorP");
            var Q13;
            Q13=sQuery(id+"F10.wireOp",VERTEX,"E101.MirrorP");
            var Q14;
            Q14=sQuery(id+"F10.wireOp",VERTEX,"E100.MirrorP");
            var Q15;
            Q15=sQuery(id+"F10.wireOp",VERTEX,"E99.MirrorP");
            var Q16;
            Q16=makeQuery(id+"F1.opExtrude","SWEPT_BODY",BODY,{"disambiguationData":[OSD([sQuery(id+"F0.wireOp",EDGE,"E0.bottom"),sQuery(id+"F0.wireOp",EDGE,"E0.top"),sQuery(id+"F0.wireOp",EDGE,"E0.left"),sQuery(id+"F0.wireOp",EDGE,"E0.right"),sQuery(id+"F0.wireOp",EDGE,"E1.trimOffspring"),sQuery(id+"F0.wireOp",EDGE,"E2"),sQuery(id+"F0.wireOp",EDGE,"E3"),sQuery(id+"F0.wireOp",EDGE,"E4"),sQuery(id+"F0.wireOp",EDGE,"E6.bottom"),sQuery(id+"F0.wireOp",EDGE,"E6.top"),sQuery(id+"F0.wireOp",EDGE,"E6.right")])]});
            hole(context, id + "F12", {"style" : HoleStyle.SIMPLE, "endStyle" : HoleEndStyle.BLIND, "standardTappedOrClearance" : lookupTablePath({ "fit" : "Normal (ASME)", "standard" : "ANSI", "size" : "#10", "type" : "Clearance" }), "standardBlindInLast" : lookupTablePath({ "fit" : "Free", "standard" : "ANSI", "size" : "#10", "type" : "Clearance" }), "holeDiameter" : 5.1 * mm, "majorDiameter" : 6.35 * mm, "holeDepth" : 26.06 * mm, "isTappedThrough" : true, "tappedDepth" : 22.25 * mm, "tapClearance" : 3, "locations" : qUnion([Q0, Q1, Q2, Q3, Q4, Q5, Q6, Q7, Q8, Q9, Q10, Q11, Q12, Q13, Q14, Q15]), "scope" : qUnion([Q16])});
        }
        {
            var Q0;
            Q0=makeQuery(id+"F1.opExtrude","CAP_FACE",FACE,{"disambiguationData":[OSD([sQuery(id+"F0.wireOp",EDGE,"E0.bottom"),sQuery(id+"F0.wireOp",EDGE,"E0.top"),sQuery(id+"F0.wireOp",EDGE,"E0.left"),sQuery(id+"F0.wireOp",EDGE,"E0.right"),sQuery(id+"F0.wireOp",EDGE,"E1.trimOffspring"),sQuery(id+"F0.wireOp",EDGE,"E2"),sQuery(id+"F0.wireOp",EDGE,"E3"),sQuery(id+"F0.wireOp",EDGE,"E4"),sQuery(id+"F0.wireOp",EDGE,"E6.bottom"),sQuery(id+"F0.wireOp",EDGE,"E6.top"),sQuery(id+"F0.wireOp",EDGE,"E6.right")])],"isStart":false});
            var sketch = newSketch(context, id + "F13", { "sketchPlane" : qUnion([Q0])});
            skCircle(sketch, "E104", {"center": v(-914.4, 723.9) * mm, "radius": 38.1 * mm});
            skCircle(sketch, "E105", {"center": v(-914.4, 520.7) * mm, "radius": 38.1 * mm});
            skCircle(sketch, "E106", {"center": v(-914.4, 292.1) * mm, "radius": 38.1 * mm});
            skCircle(sketch, "E107", {"center": v(-914.4, 88.9) * mm, "radius": 38.1 * mm});
            skSolve(sketch);
        }
        {
            var Q0;
            Q0 = qSketchRegion(id + "F13", true);
            extrude(context, id + "F14", {"entities" : qUnion([Q0]), "operationType" : NewBodyOperationType.REMOVE, "oppositeDirection" : true, "depth" : 2.03 * mm, "offsetDistance" : 25.4 * mm});
        }
        {
            var Q0;
            Q0 = qSketchRegion(id + "F6", true);
            var Q1;
            Q1=makeQuery(id+"F1.opExtrude","CAP_FACE",FACE,{"disambiguationData":[OSD([sQuery(id+"F0.wireOp",EDGE,"E0.bottom"),sQuery(id+"F0.wireOp",EDGE,"E0.top"),sQuery(id+"F0.wireOp",EDGE,"E0.left"),sQuery(id+"F0.wireOp",EDGE,"E0.right"),sQuery(id+"F0.wireOp",EDGE,"E1.trimOffspring"),sQuery(id+"F0.wireOp",EDGE,"E2"),sQuery(id+"F0.wireOp",EDGE,"E3"),sQuery(id+"F0.wireOp",EDGE,"E4"),sQuery(id+"F0.wireOp",EDGE,"E6.bottom"),sQuery(id+"F0.wireOp",EDGE,"E6.top"),sQuery(id+"F0.wireOp",EDGE,"E6.right")])],"isStart":false});
            extrude(context, id + "F15", {"entities" : qUnion([Q0, Q1]), "operationType" : NewBodyOperationType.REMOVE, "oppositeDirection" : true, "depth" : 25.4 * mm, "offsetDistance" : 25.4 * mm});
        }
        {
            var Q0;
            Q0=sQuery(id+"F8.wireOp",VERTEX,"E73.MirrorP");
            var Q1;
            Q1=sQuery(id+"F8.wireOp",VERTEX,"E74.MirrorP");
            var Q2;
            Q2=sQuery(id+"F8.wireOp",VERTEX,"E75.MirrorP");
            var Q3;
            Q3=sQuery(id+"F8.wireOp",VERTEX,"E72");
            var Q4;
            Q4=makeQuery(id+"F9.opExtrude","SWEPT_BODY",BODY,{"disambiguationData":[OSD([sQuery(id+"F8.wireOp",EDGE,"E55.bottom"),sQuery(id+"F8.wireOp",EDGE,"E55.top"),sQuery(id+"F8.wireOp",EDGE,"E55.left"),sQuery(id+"F8.wireOp",EDGE,"E55.right"),sQuery(id+"F8.wireOp",EDGE,"E61.0.left"),sQuery(id+"F8.wireOp",EDGE,"E61.0.right"),sQuery(id+"F8.wireOp",EDGE,"E61.1.startCap"),sQuery(id+"F8.wireOp",EDGE,"E61.1.endCap"),sQuery(id+"F8.wireOp",EDGE,"E61.1.left"),sQuery(id+"F8.wireOp",EDGE,"E61.1.right"),sQuery(id+"F8.wireOp",EDGE,"E64.0.left"),sQuery(id+"F8.wireOp",EDGE,"E64.0.right"),sQuery(id+"F8.wireOp",EDGE,"E64.1.startCap"),sQuery(id+"F8.wireOp",EDGE,"E64.1.endCap"),sQuery(id+"F8.wireOp",EDGE,"E64.1.left"),sQuery(id+"F8.wireOp",EDGE,"E64.1.right"),sQuery(id+"F8.wireOp",EDGE,"E67.0.left"),sQuery(id+"F8.wireOp",EDGE,"E67.0.right"),sQuery(id+"F8.wireOp",EDGE,"E67.1.startCap"),sQuery(id+"F8.wireOp",EDGE,"E67.1.endCap"),sQuery(id+"F8.wireOp",EDGE,"E67.1.left"),sQuery(id+"F8.wireOp",EDGE,"E67.1.right"),sQuery(id+"F8.wireOp",EDGE,"E70.0.left"),sQuery(id+"F8.wireOp",EDGE,"E70.0.right"),sQuery(id+"F8.wireOp",EDGE,"E70.1.startCap"),sQuery(id+"F8.wireOp",EDGE,"E70.1.endCap"),sQuery(id+"F8.wireOp",EDGE,"E70.1.left"),sQuery(id+"F8.wireOp",EDGE,"E70.1.right")])]});
            hole(context, id + "F16", {"style" : HoleStyle.SIMPLE, "endStyle" : HoleEndStyle.BLIND, "oppositeDirection" : true, "standardTappedOrClearance" : lookupTablePath({ "standard" : "ANSI", "engagement" : "75%", "pitch" : "20 tpi", "size" : "1/4", "type" : "Tapped" }), "standardBlindInLast" : lookupTablePath({ "standard" : "ANSI", "engagement" : "75%", "pitch" : "20 tpi", "size" : "1/4", "type" : "Tapped" }), "holeDiameter" : 5.1 * mm, "majorDiameter" : 6.35 * mm, "showTappedDepth" : true, "holeDepth" : 26.06 * mm, "isTappedThrough" : true, "tappedDepth" : 22.25 * mm, "tapClearance" : 3, "locations" : qUnion([Q0, Q1, Q2, Q3]), "scope" : qUnion([Q4])});
        }
        {
            var Q0;
            Q0=makeQuery(id+"F1.opExtrude","CAP_FACE",FACE,{"disambiguationData":[OSD([sQuery(id+"F0.wireOp",EDGE,"E0.bottom"),sQuery(id+"F0.wireOp",EDGE,"E0.top"),sQuery(id+"F0.wireOp",EDGE,"E0.left"),sQuery(id+"F0.wireOp",EDGE,"E0.right"),sQuery(id+"F0.wireOp",EDGE,"E1.trimOffspring"),sQuery(id+"F0.wireOp",EDGE,"E2"),sQuery(id+"F0.wireOp",EDGE,"E3"),sQuery(id+"F0.wireOp",EDGE,"E4"),sQuery(id+"F0.wireOp",EDGE,"E6.left")])],"isStart":true});
            var sketch = newSketch(context, id + "F17", { "sketchPlane" : qUnion([Q0])});
            skLineSegment(sketch, "E108", {"start": v(1143, 812.8) * mm, "end": v(1143, 0) * mm, "construction": true});
            skLineSegment(sketch, "E109", {"start": v(0, 406.4) * mm, "end": v(1219.2, 406.4) * mm, "construction": true});
            skPoint(sketch, "E110", {"position": v(1206.5, 800.1) * mm});
            skPoint(sketch, "E111.MirrorP", {"position": v(1079.5, 800.1) * mm});
            skPoint(sketch, "E112.MirrorP", {"position": v(1079.5, 12.7) * mm});
            skPoint(sketch, "E113.MirrorP", {"position": v(1206.5, 12.7) * mm});
            skSolve(sketch);
        }
        {
            var Q0;
            Q0=sQuery(id+"F17.wireOp",VERTEX,"E110");
            var Q1;
            Q1=sQuery(id+"F17.wireOp",VERTEX,"E111.MirrorP");
            var Q2;
            Q2=sQuery(id+"F17.wireOp",VERTEX,"E113.MirrorP");
            var Q3;
            Q3=sQuery(id+"F17.wireOp",VERTEX,"E112.MirrorP");
            var Q4;
            Q4=makeQuery(id+"F1.opExtrude","SWEPT_BODY",BODY,{"disambiguationData":[OSD([sQuery(id+"F0.wireOp",EDGE,"E0.bottom"),sQuery(id+"F0.wireOp",EDGE,"E0.top"),sQuery(id+"F0.wireOp",EDGE,"E0.left"),sQuery(id+"F0.wireOp",EDGE,"E0.right"),sQuery(id+"F0.wireOp",EDGE,"E1.trimOffspring"),sQuery(id+"F0.wireOp",EDGE,"E2"),sQuery(id+"F0.wireOp",EDGE,"E3"),sQuery(id+"F0.wireOp",EDGE,"E4"),sQuery(id+"F0.wireOp",EDGE,"E6.left")])]});
            hole(context, id + "F18", {"style" : HoleStyle.SIMPLE, "endStyle" : HoleEndStyle.THROUGH, "standardTappedOrClearance" : lookupTablePath({ "fit" : "Normal (ASME)", "standard" : "ANSI", "size" : "1/4", "type" : "Clearance" }), "standardBlindInLast" : lookupTablePath({ "fit" : "Free", "standard" : "ANSI", "size" : "1/4", "type" : "Clearance" }), "holeDiameter" : 6.76 * mm, "majorDiameter" : 6.35 * mm, "isTappedThrough" : true, "tappedDepth" : 22.25 * mm, "tapClearance" : 3, "locations" : qUnion([Q0, Q1, Q2, Q3]), "scope" : qUnion([Q4])});
        }
        {
            var Q0;
            Q0=qCreatedBy(makeId("Front.planeOp"),FACE);
            var sketch = newSketch(context, id + "F19", { "sketchPlane" : qUnion([Q0])});
            skLineSegment(sketch, "E114.bottom", {"start": v(0, -76.2) * mm, "end": v(393.7, -76.2) * mm});
            skLineSegment(sketch, "E114.top", {"start": v(0, -889) * mm, "end": v(393.7, -889) * mm});
            skLineSegment(sketch, "E114.left", {"start": v(0, -76.2) * mm, "end": v(0, -889) * mm});
            skLineSegment(sketch, "E115", {"start": v(0, -482.6) * mm, "end": v(989.9, -482.6) * mm, "construction": true});
            skLineSegment(sketch, "E116", {"start": v(393.7, -889) * mm, "end": v(628.34, -482.6) * mm});
            skLineSegment(sketch, "E117", {"start": v(628.34, -482.6) * mm, "end": v(393.7, -76.2) * mm});
            skPoint(sketch, "E118", {"position": v(25.4, -88.9) * mm});
            skPoint(sketch, "E119", {"position": v(279.4, -88.9) * mm});
            skPoint(sketch, "E120", {"position": v(12.7, -409.58) * mm});
            skPoint(sketch, "E121", {"position": v(25.4, -409.58) * mm});
            skPoint(sketch, "E122", {"position": v(260.05, -482.6) * mm});
            skPoint(sketch, "E123", {"position": v(514.05, -482.6) * mm});
            skCircle(sketch, "E124", {"center": v(381, -482.6) * mm, "radius": 25.4 * mm});
            skPoint(sketch, "E125.MirrorP", {"position": v(25.4, -555.63) * mm});
            skPoint(sketch, "E126.MirrorP", {"position": v(12.7, -555.63) * mm});
            skPoint(sketch, "E127.MirrorP", {"position": v(279.4, -876.3) * mm});
            skPoint(sketch, "E128.MirrorP", {"position": v(25.4, -876.3) * mm});
            skLineSegment(sketch, "E129", {"start": v(355.6, -889) * mm, "end": v(590.24, -482.6) * mm, "construction": true});
            skLineSegment(sketch, "E130", {"start": v(370.26, -889) * mm, "end": v(604.9, -482.6) * mm, "construction": true});
            skPoint(sketch, "E131", {"position": v(399.6, -812.8) * mm});
            skPoint(sketch, "E132", {"position": v(577.4, -504.84) * mm});
            skPoint(sketch, "E133", {"position": v(588.4, -511.2) * mm});
            skPoint(sketch, "E134", {"position": v(410.6, -819.15) * mm});
            skPoint(sketch, "E135.MirrorP", {"position": v(577.4, -460.36) * mm});
            skPoint(sketch, "E136.MirrorP", {"position": v(588.4, -454) * mm});
            skPoint(sketch, "E137.MirrorP", {"position": v(399.6, -152.4) * mm});
            skPoint(sketch, "E138.MirrorP", {"position": v(410.6, -146.05) * mm});
            skLineSegment(sketch, "E139.bottom", {"start": v(0, -889) * mm, "end": v(-25.4, -889) * mm});
            skLineSegment(sketch, "E139.top", {"start": v(0, -76.2) * mm, "end": v(-25.4, -76.2) * mm});
            skLineSegment(sketch, "E139.left", {"start": v(0, -889) * mm, "end": v(0, -76.2) * mm});
            skLineSegment(sketch, "E139.right", {"start": v(-25.4, -889) * mm, "end": v(-25.4, -76.2) * mm});
            skLineSegment(sketch, "E140", {"start": v(-25.4, -876.3) * mm, "end": v(401.03, -876.3) * mm, "construction": true});
            skPoint(sketch, "E141", {"position": v(0, -876.3) * mm});
            skPoint(sketch, "E142", {"position": v(304.8, -876.3) * mm});
            skPoint(sketch, "E143.MirrorP", {"position": v(0, -88.9) * mm});
            skPoint(sketch, "E144.MirrorP", {"position": v(304.8, -88.9) * mm});
            skPoint(sketch, "E145", {"position": v(234.65, -482.6) * mm});
            skPoint(sketch, "E146", {"position": v(539.45, -482.6) * mm});
            skSolve(sketch);
        }
        {
            var Q0;
            Q0 = qSketchRegion(id + "F19", true);
            extrude(context, id + "F20", {"entities" : qUnion([Q0]), "oppositeDirection" : true, "depth" : 6.35 * mm, "offsetDistance" : 25.4 * mm});
        }
        {
            var Q0;
            Q0=sQuery(id+"F19.wireOp",VERTEX,"E121");
            var Q1;
            Q1=sQuery(id+"F19.wireOp",VERTEX,"E120");
            var Q2;
            Q2=sQuery(id+"F19.wireOp",VERTEX,"E125.MirrorP");
            var Q3;
            Q3=sQuery(id+"F19.wireOp",VERTEX,"E126.MirrorP");
            var Q4;
            Q4=sQuery(id+"F19.wireOp",VERTEX,"7de669f4-6633-4621-bebc-923ab3acf4710.MirrorP");
            var Q5;
            Q5=sQuery(id+"F19.wireOp",VERTEX,"fb27b571-f7c0-46ac-8a71-9e7121acc4840.MirrorP");
            var Q6;
            Q6=sQuery(id+"F19.wireOp",VERTEX,"43e849c1-05db-4e2e-ae9d-12d70ae66a720.MirrorP");
            var Q7;
            Q7=sQuery(id+"F19.wireOp",VERTEX,"c8cac219-e8ec-4df4-94a6-b85e692b71c50.MirrorP");
            var Q8;
            Q8=sQuery(id+"F19.wireOp",VERTEX,"47355bc9-ca11-4c6f-bfe0-a7d9deacc151");
            var Q9;
            Q9=sQuery(id+"F19.wireOp",VERTEX,"TI6bzlB5-C7qq-4fa7-zgcl-docE0jnQtSQK.end");
            var Q10;
            Q10=sQuery(id+"F19.wireOp",VERTEX,"ANrkf0YX-YXG3-s8Iw-f73K-3fc7Eo7mBLsl.start");
            var Q11;
            Q11=sQuery(id+"F19.wireOp",VERTEX,"e2afd27b-a2a8-4288-a5cb-8a5e6b8038f9");
            var Q12;
            Q12=sQuery(id+"F19.wireOp",VERTEX,"E131");
            var Q13;
            Q13=sQuery(id+"F19.wireOp",VERTEX,"E134");
            var Q14;
            Q14=sQuery(id+"F19.wireOp",VERTEX,"E132");
            var Q15;
            Q15=sQuery(id+"F19.wireOp",VERTEX,"E133");
            var Q16;
            Q16=sQuery(id+"F19.wireOp",VERTEX,"E135.MirrorP");
            var Q17;
            Q17=sQuery(id+"F19.wireOp",VERTEX,"E136.MirrorP");
            var Q18;
            Q18=sQuery(id+"F19.wireOp",VERTEX,"E137.MirrorP");
            var Q19;
            Q19=sQuery(id+"F19.wireOp",VERTEX,"E138.MirrorP");
            var Q20;
            Q20=sQuery(id+"F19.wireOp",VERTEX,"E142");
            var Q21;
            Q21=sQuery(id+"F19.wireOp",VERTEX,"E141");
            var Q22;
            Q22=sQuery(id+"F19.wireOp",VERTEX,"E144.MirrorP");
            var Q23;
            Q23=sQuery(id+"F19.wireOp",VERTEX,"E143.MirrorP");
            var Q24;
            Q24=sQuery(id+"F19.wireOp",VERTEX,"E145");
            var Q25;
            Q25=sQuery(id+"F19.wireOp",VERTEX,"E146");
            var Q26;
            Q26=makeQuery(id+"F20.opExtrude","SWEPT_BODY",BODY,{"disambiguationData":[OSD([sQuery(id+"F19.wireOp",EDGE,"E114.bottom"),sQuery(id+"F19.wireOp",EDGE,"E114.top"),sQuery(id+"F19.wireOp",EDGE,"E114.left"),sQuery(id+"F19.wireOp",EDGE,"E116"),sQuery(id+"F19.wireOp",EDGE,"E117"),sQuery(id+"F19.wireOp",EDGE,"E124")])]});
            hole(context, id + "F21", {"style" : HoleStyle.SIMPLE, "endStyle" : HoleEndStyle.BLIND, "holeDiameter" : 6.76 * mm, "majorDiameter" : 6.35 * mm, "holeDepth" : 26.06 * mm, "isTappedThrough" : true, "tappedDepth" : 22.25 * mm, "tapClearance" : 3, "locations" : qUnion([Q0, Q1, Q2, Q3, Q4, Q5, Q6, Q7, Q8, Q9, Q10, Q11, Q12, Q13, Q14, Q15, Q16, Q17, Q18, Q19, Q20, Q21, Q22, Q23, Q24, Q25]), "scope" : qUnion([Q26])});
        }
    });
